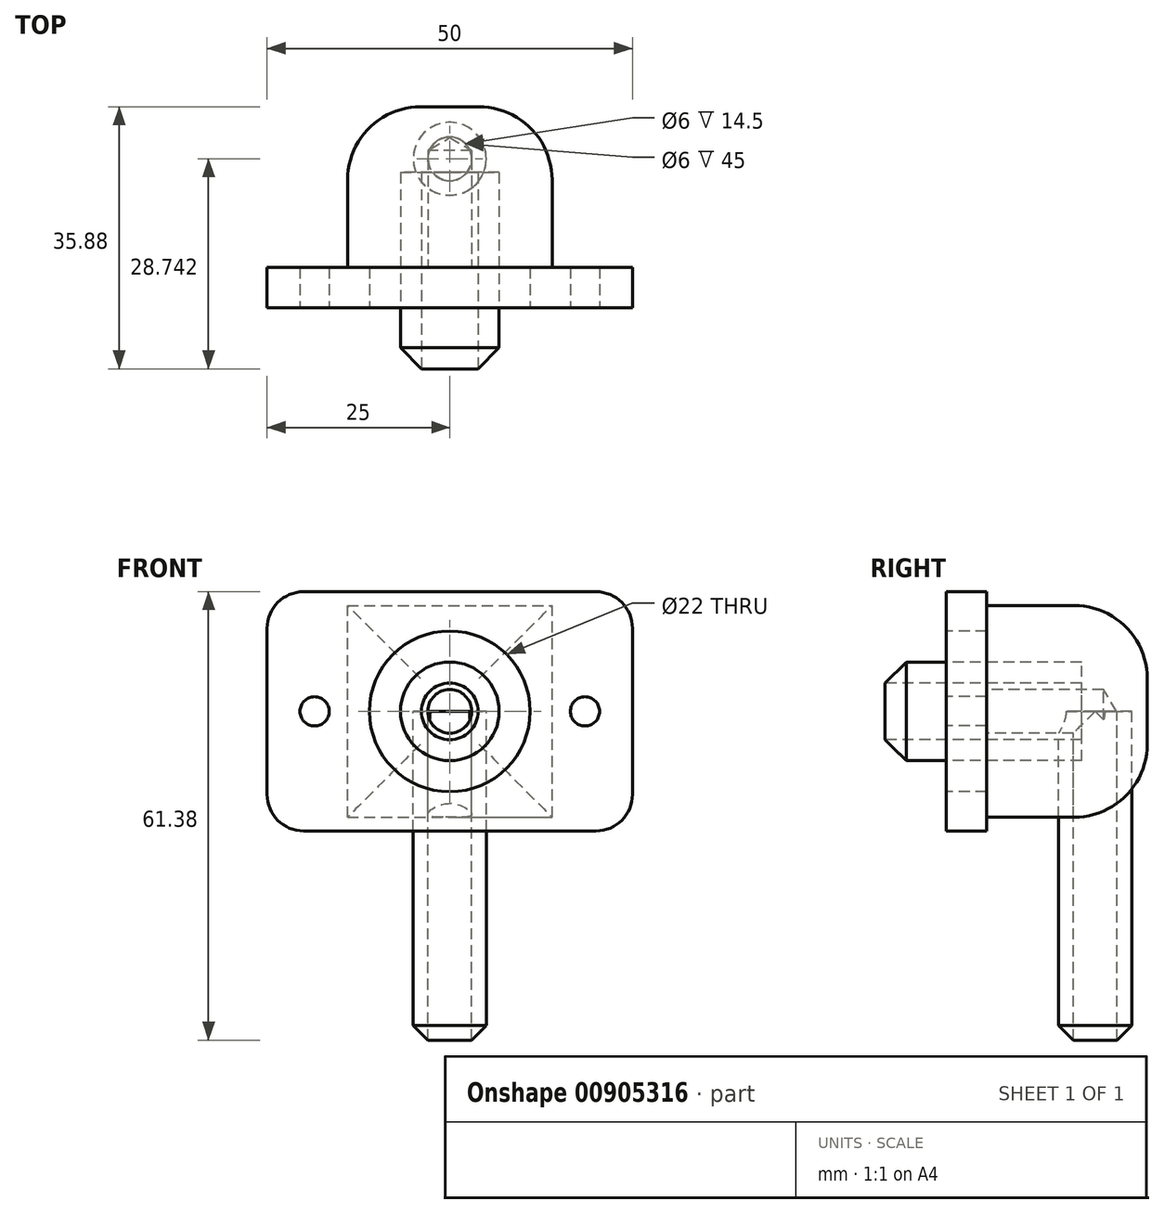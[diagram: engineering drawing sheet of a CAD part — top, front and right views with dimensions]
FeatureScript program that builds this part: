
annotation { "Feature Type Name" : "Feature", "Feature Type Description" : "" }
export const myFeature = defineFeature(function(context is Context, id is Id, definition is map)
    precondition{}
    {
        {
            var Q0;
            Q0=qCreatedBy(makeId("Front.planeOp"),FACE);
            var sketch = newSketch(context, id + "F0", { "sketchPlane" : qUnion([Q0])});
            skLineSegment(sketch, "E0.bottom", {"start": v(25, -16.37) * mm, "end": v(-25, -16.38) * mm});
            skLineSegment(sketch, "E0.top", {"start": v(25, 16.38) * mm, "end": v(-25, 16.37) * mm});
            skLineSegment(sketch, "E0.left", {"start": v(25, -16.37) * mm, "end": v(25, 16.38) * mm});
            skLineSegment(sketch, "E0.right", {"start": v(-25, -16.38) * mm, "end": v(-25, 16.38) * mm});
            skPoint(sketch, "E0.middle", {"position": v(0, 0) * mm});
            skSolve(sketch);
        }
        {
            var Q0;
            Q0 = qSketchRegion(id + "F0", true);
            extrude(context, id + "F1", {"entities" : qUnion([Q0]), "flatOperationType" : FlatOperationType.REMOVE, "depth" : 5.5 * mm, "offsetDistance" : 25 * mm, "domain" : OperationDomain.MODEL});
        }
        {
            var Q0;
            Q0=makeQuery(id+"F1.opExtrude","SWEPT_EDGE",EDGE,{"disambiguationData":[OSD([sQuery(id+"F0.wireOp",EDGE,"E0.top"),sQuery(id+"F0.wireOp",EDGE,"E0.right")])]});
            var Q1;
            Q1=makeQuery(id+"F1.opExtrude","SWEPT_EDGE",EDGE,{"disambiguationData":[OSD([sQuery(id+"F0.wireOp",EDGE,"E0.top"),sQuery(id+"F0.wireOp",EDGE,"E0.left")])]});
            var Q2;
            Q2=makeQuery(id+"F1.opExtrude","SWEPT_EDGE",EDGE,{"disambiguationData":[OSD([sQuery(id+"F0.wireOp",EDGE,"E0.bottom"),sQuery(id+"F0.wireOp",EDGE,"E0.left")])]});
            var Q3;
            Q3=makeQuery(id+"F1.opExtrude","SWEPT_EDGE",EDGE,{"disambiguationData":[OSD([sQuery(id+"F0.wireOp",EDGE,"E0.bottom"),sQuery(id+"F0.wireOp",EDGE,"E0.right")])]});
            fillet(context, id + "F2", {"entities" : qUnion([Q0, Q1, Q2, Q3]), "radius" : 5 * mm, "tangentPropagation" : true, "allowEdgeOverflow" : false});
        }
        {
            var Q0;
            Q0=makeQuery(id+"F1.opExtrude","CAP_FACE",FACE,{"disambiguationData":[OSD([sQuery(id+"F0.wireOp",EDGE,"E0.bottom"),sQuery(id+"F0.wireOp",EDGE,"E0.top"),sQuery(id+"F0.wireOp",EDGE,"E0.left"),sQuery(id+"F0.wireOp",EDGE,"E0.right")])],"isStart":false});
            var sketch = newSketch(context, id + "F3", { "sketchPlane" : qUnion([Q0])});
            skCircle(sketch, "E1", {"center": v(-81.37, 0) * mm, "radius": 7.13 * mm});
            skCircle(sketch, "E2", {"center": v(18.5, 0) * mm, "radius": 2 * mm});
            skCircle(sketch, "E3", {"center": v(-18.5, 0) * mm, "radius": 2 * mm});
            skCircle(sketch, "E4", {"center": v(0, 0) * mm, "radius": 11 * mm});
            skCircle(sketch, "E5", {"center": v(0, 0) * mm, "radius": 6.75 * mm});
            skCircle(sketch, "E6", {"center": v(0, 0) * mm, "radius": 3.88 * mm});
            skSolve(sketch);
        }
        {
            var Q0;
            Q0=makeQuery(id+"F3.imprint","IMPRINT",FACE,{"disambiguationData":[TD([[makeQuery(id+"F3.imprint","IMPRINT",EDGE,{"derivedFrom":sQuery(id+"F3.wireOp",EDGE,"E6")}),1.0]])]});
            extrude(context, id + "F4", {"entities" : qUnion([Q0]), "operationType" : NewBodyOperationType.REMOVE, "oppositeDirection" : true, "depth" : 10 * mm, "offsetDistance" : 25 * mm});
        }
        {
            var Q0;
            Q0 = qSketchRegion(id + "F3", true);
            extrude(context, id + "F5", {"entities" : qUnion([Q0]), "operationType" : NewBodyOperationType.REMOVE, "flatOperationType" : FlatOperationType.REMOVE, "oppositeDirection" : true, "depth" : 20 * mm, "offsetDistance" : 25 * mm, "domain" : OperationDomain.MODEL});
        }
        {
            var Q0;
            Q0=makeQuery(id+"F5.boolean.opBoolean","SPLIT",FACE,{"disambiguationData":[TD([makeQuery(id+"F4.boolean.opBoolean","COPY",FACE,{"derivedFrom":makeQuery(id+"F4.opExtrude","SWEPT_FACE",FACE,{"disambiguationData":[OSD([sQuery(id+"F3.wireOp",EDGE,"E6")])]})})])],"derivedFrom":makeQuery(id+"F1.opExtrude","CAP_FACE",FACE,{"disambiguationData":[OSD([sQuery(id+"F0.wireOp",EDGE,"E0.bottom"),sQuery(id+"F0.wireOp",EDGE,"E0.top"),sQuery(id+"F0.wireOp",EDGE,"E0.left"),sQuery(id+"F0.wireOp",EDGE,"E0.right")])],"isStart":true})});
            extrude(context, id + "F6", {"entities" : qUnion([Q0]), "operationType" : NewBodyOperationType.ADD, "depth" : 13 * mm, "offsetDistance" : 25 * mm, "hasSecondDirection" : true, "secondDirectionOppositeDirection" : true, "secondDirectionDepth" : 14 * mm});
        }
        {
            var Q0;
            Q0=makeQuery(id+"F6.opExtrude","CAP_EDGE",EDGE,{"disambiguationData":[OSD([sQuery(id+"F0.wireOp",EDGE,"E0.bottom"),sQuery(id+"F0.wireOp",EDGE,"E0.top"),sQuery(id+"F0.wireOp",EDGE,"E0.left"),sQuery(id+"F0.wireOp",EDGE,"E0.right"),sQuery(id+"F3.wireOp",EDGE,"E5")])],"isStart":true});
            chamfer(context, id + "F7", {"entities" : qUnion([Q0]), "width" : 3 * mm, "tangentPropagation" : true});
        }
        {
            var Q0;
            Q0=qCreatedBy(makeId("Front.planeOp"),FACE);
            var sketch = newSketch(context, id + "F8", { "sketchPlane" : qUnion([Q0])});
            skLineSegment(sketch, "E7.bottom", {"start": v(-14, -14.5) * mm, "end": v(14, -14.5) * mm});
            skLineSegment(sketch, "E7.top", {"start": v(-14, 14.5) * mm, "end": v(14, 14.5) * mm});
            skLineSegment(sketch, "E7.left", {"start": v(-14, -14.5) * mm, "end": v(-14, 14.5) * mm});
            skLineSegment(sketch, "E7.right", {"start": v(14, -14.5) * mm, "end": v(14, 14.5) * mm});
            skPoint(sketch, "E7.middle", {"position": v(0, 0) * mm});
            skSolve(sketch);
        }
        {
            var Q0;
            Q0 = qSketchRegion(id + "F8", true);
            extrude(context, id + "F9", {"entities" : qUnion([Q0]), "oppositeDirection" : true, "depth" : 22 * mm, "offsetDistance" : 25 * mm});
        }
        {
            var Q0;
            Q0=qCreatedBy(makeId("Top.planeOp"),FACE);
            var sketch = newSketch(context, id + "F10", { "sketchPlane" : qUnion([Q0])});
            skCircle(sketch, "E8", {"center": v(0, 14.86) * mm, "radius": 5 * mm});
            skCircle(sketch, "E9", {"center": v(0, 14.86) * mm, "radius": 3 * mm});
            skSolve(sketch);
        }
        {
            var Q0;
            Q0=sQuery(id+"F10.wireOp",VERTEX,"E8.center");
            var Q1;
            Q1=makeQuery(id+"F9.opExtrude","SWEPT_BODY",BODY,{"disambiguationData":[OSD([sQuery(id+"F8.wireOp",EDGE,"E7.bottom"),sQuery(id+"F8.wireOp",EDGE,"E7.top"),sQuery(id+"F8.wireOp",EDGE,"E7.left"),sQuery(id+"F8.wireOp",EDGE,"E7.right")])]});
            hole(context, id + "F11", {"style" : HoleStyle.SIMPLE, "endStyle" : HoleEndStyle.BLIND, "holeDiameter" : 6 * mm, "majorDiameter" : 5 * mm, "holeDepth" : 45 * mm, "isTappedThrough" : true, "tappedDepth" : 12 * mm, "tapClearance" : 3, "locations" : qUnion([Q0]), "scope" : qUnion([Q1])});
        }
        {
            var Q0;
            Q0 = qSketchRegion(id + "F10", true);
            extrude(context, id + "F12", {"entities" : qUnion([Q0]), "flatOperationType" : FlatOperationType.REMOVE, "oppositeDirection" : true, "depth" : 45 * mm, "offsetDistance" : 25 * mm, "domain" : OperationDomain.MODEL});
        }
        {
            var Q0;
            Q0=makeQuery(id+"F9.opExtrude","CAP_EDGE",EDGE,{"disambiguationData":[OSD([sQuery(id+"F8.wireOp",EDGE,"E7.left")])],"isStart":false});
            var Q1;
            Q1=makeQuery(id+"F9.opExtrude","CAP_EDGE",EDGE,{"disambiguationData":[OSD([sQuery(id+"F8.wireOp",EDGE,"E7.top")])],"isStart":false});
            var Q2;
            Q2=makeQuery(id+"F9.opExtrude","CAP_EDGE",EDGE,{"disambiguationData":[OSD([sQuery(id+"F8.wireOp",EDGE,"E7.right")])],"isStart":false});
            var Q3;
            Q3=makeQuery(id+"F9.opExtrude","CAP_FACE",FACE,{"disambiguationData":[OSD([sQuery(id+"F8.wireOp",EDGE,"E7.bottom"),sQuery(id+"F8.wireOp",EDGE,"E7.top"),sQuery(id+"F8.wireOp",EDGE,"E7.left"),sQuery(id+"F8.wireOp",EDGE,"E7.right")])],"isStart":false});
            fillet(context, id + "F13", {"entities" : qUnion([Q0, Q1, Q2, Q3]), "radius" : 10 * mm, "tangentPropagation" : true, "allowEdgeOverflow" : false});
        }
        {
            var Q0;
            Q0=qCreatedBy(makeId("Front.planeOp"),FACE);
            var sketch = newSketch(context, id + "F14", { "sketchPlane" : qUnion([Q0])});
            skCircle(sketch, "E10", {"center": v(0, 0) * mm, "radius": 3.72 * mm});
            skSolve(sketch);
        }
        {
            var Q0;
            Q0=sQuery(id+"F14.wireOp",VERTEX,"E10.center");
            var Q1;
            Q1=makeQuery(id+"F12.opExtrude","SWEPT_BODY",BODY,{"disambiguationData":[OSD([sQuery(id+"F10.wireOp",EDGE,"E8"),sQuery(id+"F10.wireOp",EDGE,"E9")])]});
            var Q2;
            Q2=makeQuery(id+"F9.opExtrude","SWEPT_BODY",BODY,{"disambiguationData":[OSD([sQuery(id+"F8.wireOp",EDGE,"E7.bottom"),sQuery(id+"F8.wireOp",EDGE,"E7.top"),sQuery(id+"F8.wireOp",EDGE,"E7.left"),sQuery(id+"F8.wireOp",EDGE,"E7.right")])]});
            hole(context, id + "F15", {"style" : HoleStyle.SIMPLE, "endStyle" : HoleEndStyle.BLIND, "holeDiameter" : 6 * mm, "majorDiameter" : 5 * mm, "holeDepth" : 16 * mm, "isTappedThrough" : true, "tappedDepth" : 12 * mm, "tapClearance" : 3, "startFromSketch" : true, "locations" : qUnion([Q0]), "scope" : qUnion([Q1, Q2])});
        }
        {
            var Q0;
            Q0=makeQuery(id+"F12.opExtrude","CAP_EDGE",EDGE,{"disambiguationData":[OSD([sQuery(id+"F10.wireOp",EDGE,"E8")])],"isStart":false});
            chamfer(context, id + "F16", {"entities" : qUnion([Q0]), "width" : 2 * mm, "tangentPropagation" : true});
        }
    });
